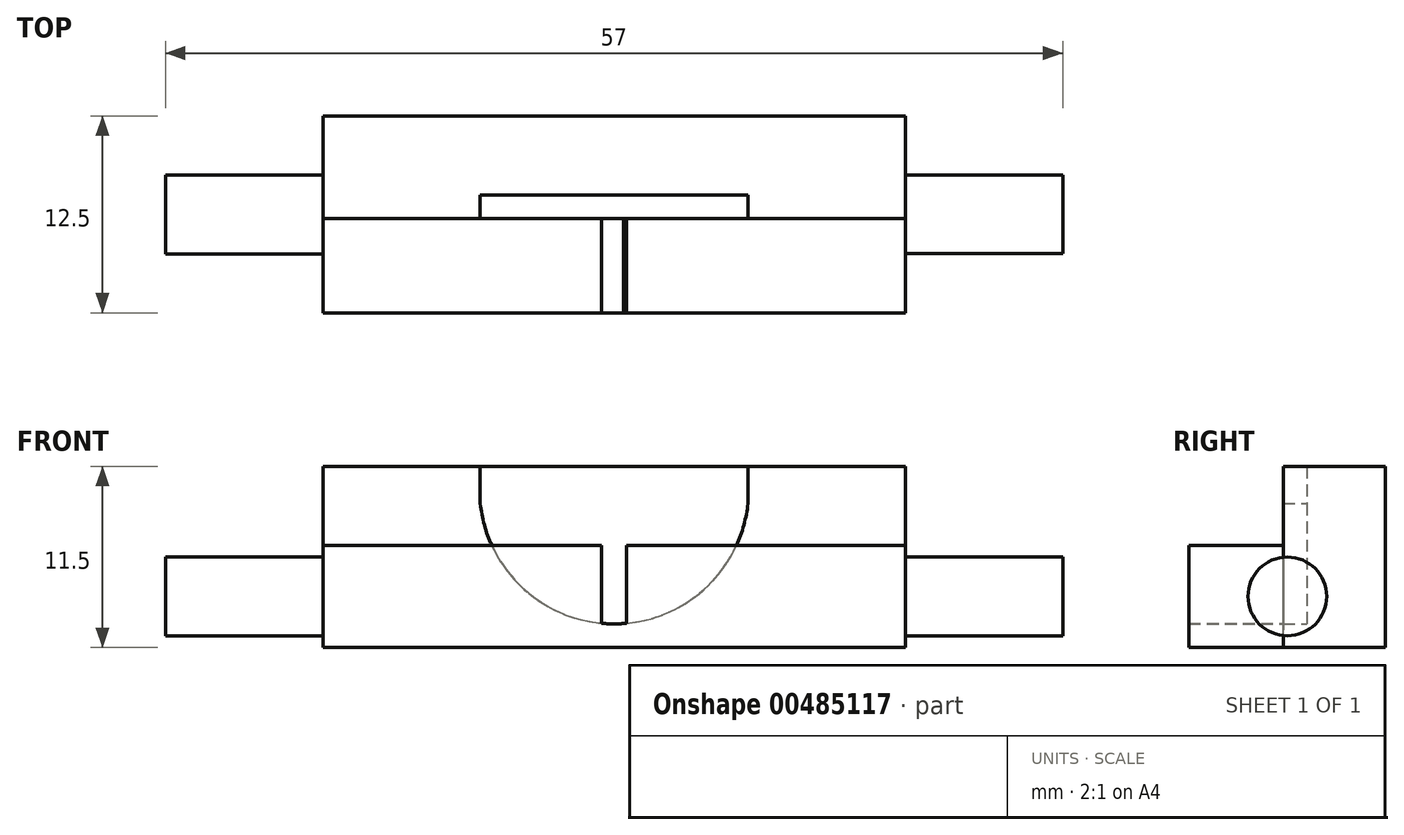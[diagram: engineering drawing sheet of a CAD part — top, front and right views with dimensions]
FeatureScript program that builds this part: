
annotation { "Feature Type Name" : "Feature", "Feature Type Description" : "" }
export const myFeature = defineFeature(function(context is Context, id is Id, definition is map)
    precondition{}
    {
        {
            var Q0;
            Q0=qCreatedBy(makeId("Front.planeOp"),FACE);
            var sketch = newSketch(context, id + "F0", { "sketchPlane" : qUnion([Q0])});
            skLineSegment(sketch, "E0.bottom", {"start": v(-8.5, 7.64) * mm, "end": v(8.5, 7.64) * mm, "construction": true});
            skLineSegment(sketch, "E0.top", {"start": v(-8.5, -7.64) * mm, "end": v(8.5, -7.64) * mm, "construction": true});
            skLineSegment(sketch, "E0.left", {"start": v(-8.5, 7.64) * mm, "end": v(-8.5, -7.64) * mm, "construction": true});
            skLineSegment(sketch, "E0.right", {"start": v(8.5, 7.64) * mm, "end": v(8.5, -7.64) * mm, "construction": true});
            skPoint(sketch, "E0.middle", {"position": v(0, 0) * mm});
            skLineSegment(sketch, "E1", {"start": v(0, 7.64) * mm, "end": v(0, -7.64) * mm, "construction": true});
            skLineSegment(sketch, "E2", {"start": v(-8.5, 0) * mm, "end": v(8.5, 0) * mm, "construction": true});
            skArc(sketch, "E3", {"start": v(-8.5, 0) * mm, "mid": v(0, -7.64) * mm, "end": v(8.5, 0) * mm});
            skLineSegment(sketch, "E4.bottom", {"start": v(-8.5, 7.64) * mm, "end": v(-20.5, 7.64) * mm, "construction": true});
            skLineSegment(sketch, "E4.top", {"start": v(-8.5, -7.64) * mm, "end": v(-20.5, -7.64) * mm, "construction": true});
            skLineSegment(sketch, "E4.right", {"start": v(-20.5, 7.64) * mm, "end": v(-20.5, -7.64) * mm, "construction": true});
            skLineSegment(sketch, "E5.bottom", {"start": v(8.5, 7.64) * mm, "end": v(20.5, 7.64) * mm, "construction": true});
            skLineSegment(sketch, "E5.top", {"start": v(8.5, -7.64) * mm, "end": v(20.5, -7.64) * mm, "construction": true});
            skLineSegment(sketch, "E5.right", {"start": v(20.5, 7.64) * mm, "end": v(20.5, -7.64) * mm, "construction": true});
            skLineSegment(sketch, "E6", {"start": v(-20.5, 2.36) * mm, "end": v(20.5, 2.36) * mm, "construction": true});
            skLineSegment(sketch, "E7", {"start": v(-18.5, 7.64) * mm, "end": v(-18.5, -7.64) * mm, "construction": true});
            skLineSegment(sketch, "E8", {"start": v(18.5, 7.64) * mm, "end": v(18.5, -7.64) * mm, "construction": true});
            skLineSegment(sketch, "E9.bottom", {"start": v(-20.5, -7.64) * mm, "end": v(20.5, -7.64) * mm, "construction": true});
            skLineSegment(sketch, "E9.top", {"start": v(-20.5, -9.14) * mm, "end": v(20.5, -9.14) * mm, "construction": true});
            skLineSegment(sketch, "E9.left", {"start": v(-20.5, -7.64) * mm, "end": v(-20.5, -9.14) * mm, "construction": true});
            skLineSegment(sketch, "E9.right", {"start": v(20.5, -7.64) * mm, "end": v(20.5, -9.14) * mm, "construction": true});
            skLineSegment(sketch, "E10", {"start": v(-18.5, 2.36) * mm, "end": v(-18.5, -9.14) * mm});
            skLineSegment(sketch, "E11", {"start": v(-18.5, -9.14) * mm, "end": v(18.5, -9.14) * mm});
            skLineSegment(sketch, "E12", {"start": v(18.5, -9.14) * mm, "end": v(18.5, 2.36) * mm});
            skLineSegment(sketch, "E13", {"start": v(18.5, 2.36) * mm, "end": v(8.5, 2.36) * mm});
            skLineSegment(sketch, "E14", {"start": v(8.5, 2.36) * mm, "end": v(8.5, 0) * mm});
            skLineSegment(sketch, "E15", {"start": v(-18.5, 2.36) * mm, "end": v(-8.5, 2.36) * mm});
            skLineSegment(sketch, "E16", {"start": v(-8.5, 2.36) * mm, "end": v(-8.5, 0) * mm});
            skLineSegment(sketch, "E17", {"start": v(-8.5, 2.36) * mm, "end": v(8.5, 2.36) * mm});
            skLineSegment(sketch, "E18", {"start": v(-20.5, 7.64) * mm, "end": v(-20.5, -7.64) * mm});
            skLineSegment(sketch, "E19", {"start": v(-20.5, -7.64) * mm, "end": v(-20.5, -9.14) * mm});
            skLineSegment(sketch, "E20", {"start": v(-18.5, -9.14) * mm, "end": v(-20.5, -9.14) * mm});
            skLineSegment(sketch, "E21", {"start": v(20.5, -9.14) * mm, "end": v(18.5, -9.14) * mm});
            skLineSegment(sketch, "E22", {"start": v(20.5, -9.14) * mm, "end": v(20.5, 2.36) * mm});
            skLineSegment(sketch, "E23", {"start": v(18.5, 2.36) * mm, "end": v(20.5, 2.36) * mm});
            skLineSegment(sketch, "E24", {"start": v(-18.5, 2.36) * mm, "end": v(-20.5, 2.36) * mm});
            skLineSegment(sketch, "E25", {"start": v(-20.5, 2.36) * mm, "end": v(-20.5, -9.14) * mm});
            skSolve(sketch);
        }
        {
            var Q0;
            Q0=makeQuery(id+"F0.imprint","IMPRINT",FACE,{"disambiguationData":[TD([[makeQuery(id+"F0.imprint","IMPRINT",EDGE,{"derivedFrom":sQuery(id+"F0.wireOp",EDGE,"E3")}),1.0]])]});
            extrude(context, id + "F1", {"entities" : qUnion([Q0]), "depth" : 5 * mm});
        }
        {
            var Q0;
            Q0=makeQuery(id+"F0.imprint","IMPRINT",FACE,{"disambiguationData":[TD([[makeQuery(id+"F0.imprint","IMPRINT",EDGE,{"derivedFrom":sQuery(id+"F0.wireOp",EDGE,"E3")}),-1.0]])]});
            extrude(context, id + "F2", {"entities" : qUnion([Q0]), "operationType" : NewBodyOperationType.ADD, "depth" : 6.5 * mm});
        }
        {
            var Q0;
            Q0=makeQuery(id+"F2.opExtrude","CAP_FACE",FACE,{"disambiguationData":[OSD([sQuery(id+"F0.wireOp",EDGE,"E3"),sQuery(id+"F0.wireOp",EDGE,"E10"),sQuery(id+"F0.wireOp",EDGE,"E11"),sQuery(id+"F0.wireOp",EDGE,"E12"),sQuery(id+"F0.wireOp",EDGE,"E13"),sQuery(id+"F0.wireOp",EDGE,"E14"),sQuery(id+"F0.wireOp",EDGE,"E15"),sQuery(id+"F0.wireOp",EDGE,"E16")])],"isStart":false});
            var sketch = newSketch(context, id + "F3", { "sketchPlane" : qUnion([Q0])});
            skLineSegment(sketch, "E26", {"start": v(0, -7.64) * mm, "end": v(0, 0) * mm, "construction": true});
            skLineSegment(sketch, "E27", {"start": v(-18.5, 0) * mm, "end": v(-18.5, -9.14) * mm});
            skLineSegment(sketch, "E28", {"start": v(-18.5, -9.14) * mm, "end": v(18.5, -9.14) * mm});
            skLineSegment(sketch, "E29", {"start": v(18.5, -9.14) * mm, "end": v(18.5, 0) * mm});
            skLineSegment(sketch, "E30", {"start": v(0.8, -7.62) * mm, "end": v(-0.6, -7.62) * mm});
            skLineSegment(sketch, "E31", {"start": v(0, -7.64) * mm, "end": v(0, -2.67) * mm, "construction": true});
            skLineSegment(sketch, "E32.bottom", {"start": v(-0.8, -2.67) * mm, "end": v(0.8, -2.67) * mm, "construction": true});
            skLineSegment(sketch, "E32.top", {"start": v(-0.8, -7.62) * mm, "end": v(0.8, -7.62) * mm, "construction": true});
            skLineSegment(sketch, "E32.left", {"start": v(-0.8, -2.67) * mm, "end": v(-0.8, -7.62) * mm, "construction": true});
            skLineSegment(sketch, "E32.right", {"start": v(0.8, -2.67) * mm, "end": v(0.8, -7.62) * mm, "construction": true});
            skLineSegment(sketch, "E33", {"start": v(-0.8, -2.67) * mm, "end": v(-18.5, -2.67) * mm});
            skLineSegment(sketch, "E34", {"start": v(0.8, -2.67) * mm, "end": v(18.5, -2.67) * mm});
            skLineSegment(sketch, "E35", {"start": v(-0.8, -2.67) * mm, "end": v(-0.8, -7.62) * mm});
            skLineSegment(sketch, "E36", {"start": v(0.8, -7.62) * mm, "end": v(0.8, -2.67) * mm});
            skSolve(sketch);
        }
        {
            var Q0;
            {var subQ16=sQuery(id+"F3.wireOp",EDGE,"E28");Q0=makeQuery(id+"F3.imprint","IMPRINT",FACE,{"disambiguationData":[TD([[makeQuery(id+"F3.imprint","IMPRINT",EDGE,{"derivedFrom":subQ16}),1.0]])]});}
            var Q1;
            {var subQ0=sQuery(id+"F3.wireOp",EDGE,"E35");var subQ1=sQuery(id+"F3.wireOp",EDGE,"E33");var subQ2=makeQuery(id+"F3.imprint","INTERSECT",VERTEX,{"derivedFrom":[subQ1,subQ0]});Q1=makeQuery(id+"F3.imprint","IMPRINT",FACE,{"disambiguationData":[TD([[makeQuery(id+"F3.imprint","IMPRINT",EDGE,{"disambiguationData":[TD([[subQ2,-1.0]])],"derivedFrom":subQ1}),1.0]])]});}
            var Q2;
            {var subQ0=sQuery(id+"F3.wireOp",EDGE,"E36");var subQ1=sQuery(id+"F3.wireOp",EDGE,"E34");var subQ2=makeQuery(id+"F3.imprint","INTERSECT",VERTEX,{"derivedFrom":[subQ1,subQ0]});Q2=makeQuery(id+"F3.imprint","IMPRINT",FACE,{"disambiguationData":[TD([[makeQuery(id+"F3.imprint","IMPRINT",EDGE,{"disambiguationData":[TD([[subQ2,-1.0]])],"derivedFrom":subQ1}),-1.0]])]});}
            extrude(context, id + "F4", {"entities" : qUnion([Q0, Q1, Q2]), "depth" : 6 * mm});
        }
        {
            var Q0;
            Q0=makeQuery(id+"F2.opExtrude","SWEPT_FACE",FACE,{"disambiguationData":[OSD([sQuery(id+"F0.wireOp",EDGE,"E12")])]});
            var sketch = newSketch(context, id + "F5", { "sketchPlane" : qUnion([Q0])});
            skLineSegment(sketch, "E37.bottom", {"start": v(0, -9.14) * mm, "end": v(-12.48, -9.14) * mm, "construction": true});
            skLineSegment(sketch, "E37.top", {"start": v(0, -2.65) * mm, "end": v(-12.48, -2.65) * mm, "construction": true});
            skLineSegment(sketch, "E37.left", {"start": v(0, -9.14) * mm, "end": v(0, -2.65) * mm, "construction": true});
            skLineSegment(sketch, "E37.right", {"start": v(-12.48, -9.14) * mm, "end": v(-12.48, -2.65) * mm, "construction": true});
            skLineSegment(sketch, "E38", {"start": v(-12.48, -5.9) * mm, "end": v(0, -5.9) * mm, "construction": true});
            skLineSegment(sketch, "E39", {"start": v(-6.24, -9.14) * mm, "end": v(-6.24, -2.65) * mm, "construction": true});
            skCircle(sketch, "E40", {"center": v(-6.24, -5.9) * mm, "radius": 2.5 * mm});
            skSolve(sketch);
        }
        {
            var Q0;
            {var subQ0=sQuery(id+"F5.wireOp",EDGE,"E40");var subQ1=makeQuery(id+"F2.opExtrude","CAP_EDGE",EDGE,{"disambiguationData":[OSD([sQuery(id+"F0.wireOp",EDGE,"E12")])],"isStart":false});var subQ2=makeQuery(id+"F5.imprint","INTERSECT",VERTEX,{"disambiguationData":[OD(0.0)],"derivedFrom":[subQ1,subQ0]});Q0=makeQuery(id+"F5.imprint","IMPRINT",FACE,{"disambiguationData":[TD([[makeQuery(id+"F5.imprint","IMPRINT",EDGE,{"disambiguationData":[TD([[subQ2,1.0]])],"derivedFrom":subQ0}),1.0]])]});}
            var Q1;
            {var subQ0=sQuery(id+"F5.wireOp",EDGE,"E40");var subQ1=makeQuery(id+"F2.opExtrude","CAP_EDGE",EDGE,{"disambiguationData":[OSD([sQuery(id+"F0.wireOp",EDGE,"E12")])],"isStart":false});var subQ2=makeQuery(id+"F5.imprint","INTERSECT",VERTEX,{"disambiguationData":[OD(0.0)],"derivedFrom":[subQ1,subQ0]});Q1=makeQuery(id+"F5.imprint","IMPRINT",FACE,{"disambiguationData":[TD([[makeQuery(id+"F5.imprint","IMPRINT",EDGE,{"disambiguationData":[TD([[subQ2,-1.0]])],"derivedFrom":subQ0}),1.0]])]});}
            extrude(context, id + "F6", {"entities" : qUnion([Q0, Q1]), "depth" : 10 * mm, "offsetDistance" : 25 * mm});
        }
        {
            var Q0;
            Q0=makeQuery(id+"F4.opExtrude","SWEPT_FACE",FACE,{"disambiguationData":[OSD([sQuery(id+"F3.wireOp",EDGE,"E27")])]});
            var sketch = newSketch(context, id + "F7", { "sketchPlane" : qUnion([Q0])});
            skLineSegment(sketch, "E41.bottom", {"start": v(12.5, -9.14) * mm, "end": v(0, -9.14) * mm, "construction": true});
            skLineSegment(sketch, "E41.top", {"start": v(12.5, -2.67) * mm, "end": v(0, -2.67) * mm, "construction": true});
            skLineSegment(sketch, "E41.left", {"start": v(12.5, -9.14) * mm, "end": v(12.5, -2.67) * mm, "construction": true});
            skLineSegment(sketch, "E41.right", {"start": v(0, -9.14) * mm, "end": v(0, -2.67) * mm, "construction": true});
            skLineSegment(sketch, "E42", {"start": v(0, -5.9) * mm, "end": v(12.5, -5.9) * mm, "construction": true});
            skLineSegment(sketch, "E43", {"start": v(6.25, -9.14) * mm, "end": v(6.25, -2.67) * mm, "construction": true});
            skCircle(sketch, "E44", {"center": v(6.25, -5.9) * mm, "radius": 2.5 * mm});
            skSolve(sketch);
        }
        {
            var Q0;
            {var subQ0=sQuery(id+"F7.wireOp",EDGE,"E44");var subQ1=makeQuery(id+"F4.opExtrude","CAP_EDGE",EDGE,{"disambiguationData":[OSD([sQuery(id+"F3.wireOp",EDGE,"E27")])],"isStart":true});var subQ2=makeQuery(id+"F7.imprint","INTERSECT",VERTEX,{"disambiguationData":[OD(0.0)],"derivedFrom":[subQ1,subQ0]});Q0=makeQuery(id+"F7.imprint","IMPRINT",FACE,{"disambiguationData":[TD([[makeQuery(id+"F7.imprint","IMPRINT",EDGE,{"disambiguationData":[TD([[subQ2,1.0]])],"derivedFrom":subQ0}),1.0]])]});}
            var Q1;
            {var subQ0=sQuery(id+"F7.wireOp",EDGE,"E44");var subQ1=makeQuery(id+"F4.opExtrude","CAP_EDGE",EDGE,{"disambiguationData":[OSD([sQuery(id+"F3.wireOp",EDGE,"E27")])],"isStart":true});var subQ2=makeQuery(id+"F7.imprint","INTERSECT",VERTEX,{"disambiguationData":[OD(0.0)],"derivedFrom":[subQ1,subQ0]});Q1=makeQuery(id+"F7.imprint","IMPRINT",FACE,{"disambiguationData":[TD([[makeQuery(id+"F7.imprint","IMPRINT",EDGE,{"disambiguationData":[TD([[subQ2,-1.0]])],"derivedFrom":subQ0}),1.0]])]});}
            extrude(context, id + "F8", {"entities" : qUnion([Q0, Q1]), "depth" : 10 * mm, "offsetDistance" : 25 * mm});
        }
    });
